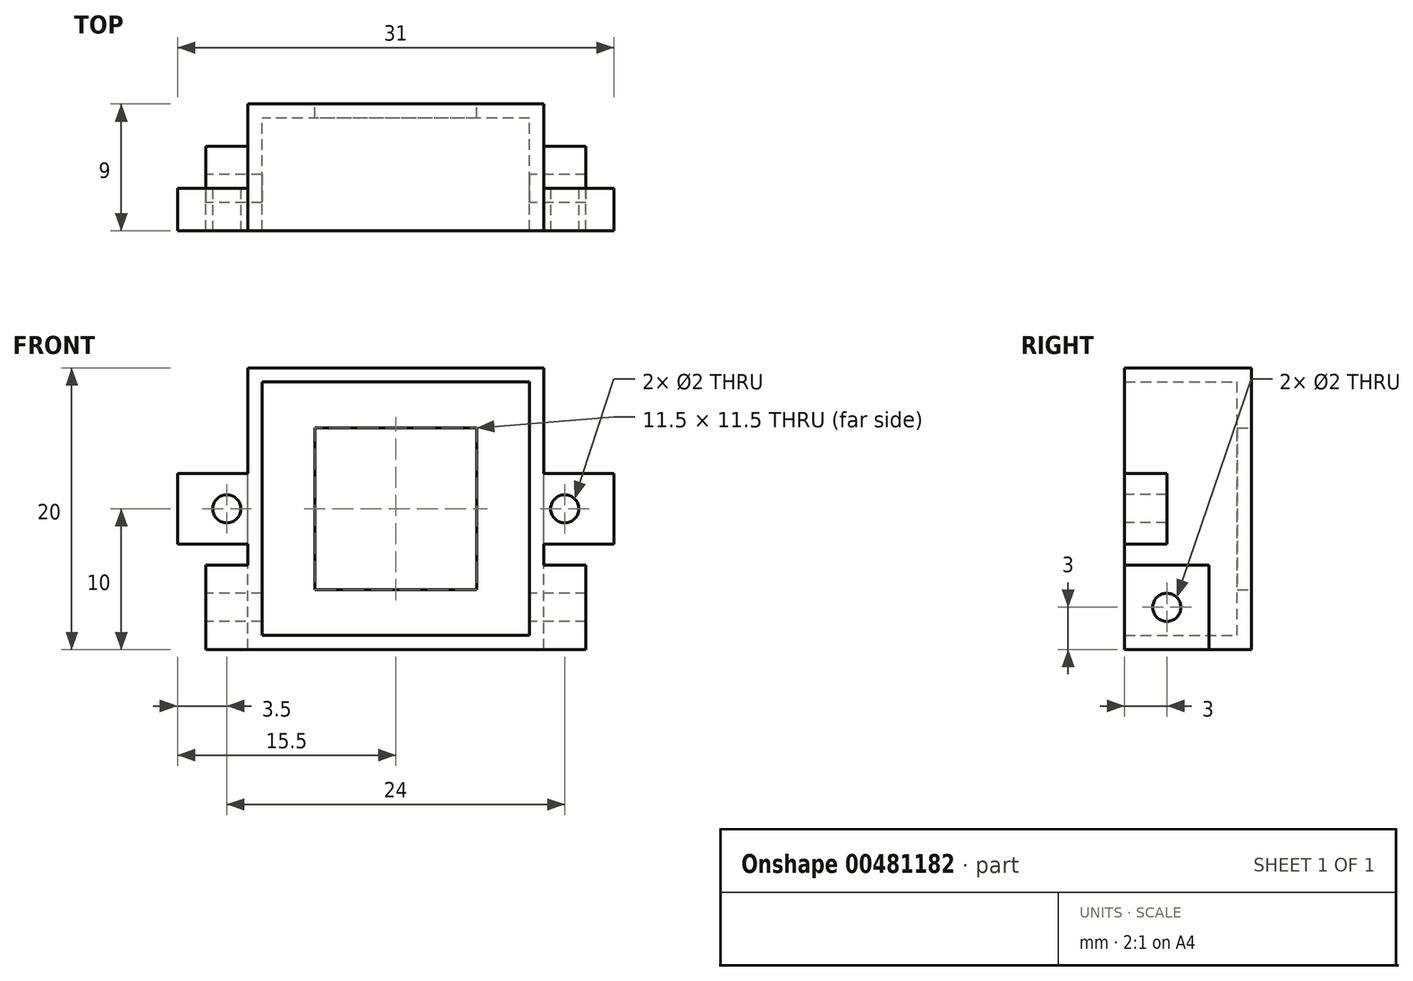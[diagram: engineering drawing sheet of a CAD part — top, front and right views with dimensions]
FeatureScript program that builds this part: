
annotation { "Feature Type Name" : "Feature", "Feature Type Description" : "" }
export const myFeature = defineFeature(function(context is Context, id is Id, definition is map)
    precondition{}
    {
        {
            var Q0;
            Q0=qCreatedBy(makeId("Front.planeOp"),FACE);
            var sketch = newSketch(context, id + "F0", { "sketchPlane" : qUnion([Q0])});
            skLineSegment(sketch, "E0.bottom", {"start": v(9, -8.5) * mm, "end": v(-9, -8.5) * mm});
            skLineSegment(sketch, "E0.top", {"start": v(9, 8.5) * mm, "end": v(-9, 8.5) * mm});
            skLineSegment(sketch, "E0.left", {"start": v(9, -8.5) * mm, "end": v(9, 8.5) * mm});
            skLineSegment(sketch, "E0.right", {"start": v(-9, -8.5) * mm, "end": v(-9, 8.5) * mm});
            skPoint(sketch, "E0.middle", {"position": v(0, 0) * mm});
            skLineSegment(sketch, "E1.bottom", {"start": v(9.5, -9) * mm, "end": v(-9.5, -9) * mm});
            skLineSegment(sketch, "E1.top", {"start": v(9.5, 9) * mm, "end": v(-9.5, 9) * mm});
            skLineSegment(sketch, "E1.left", {"start": v(9.5, -9) * mm, "end": v(9.5, 9) * mm});
            skLineSegment(sketch, "E1.right", {"start": v(-9.5, -9) * mm, "end": v(-9.5, 9) * mm});
            skLineSegment(sketch, "E2.bottom", {"start": v(10.5, -10) * mm, "end": v(-10.5, -10) * mm});
            skLineSegment(sketch, "E2.top", {"start": v(10.5, 10) * mm, "end": v(-10.5, 10) * mm});
            skLineSegment(sketch, "E2.left", {"start": v(10.5, -10) * mm, "end": v(10.5, 10) * mm});
            skLineSegment(sketch, "E2.right", {"start": v(-10.5, -10) * mm, "end": v(-10.5, 10) * mm});
            skLineSegment(sketch, "E3.bottom", {"start": v(5.75, 5.75) * mm, "end": v(-5.75, 5.75) * mm});
            skLineSegment(sketch, "E3.top", {"start": v(5.75, -5.75) * mm, "end": v(-5.75, -5.75) * mm});
            skLineSegment(sketch, "E3.left", {"start": v(5.75, 5.75) * mm, "end": v(5.75, -5.75) * mm});
            skLineSegment(sketch, "E3.right", {"start": v(-5.75, 5.75) * mm, "end": v(-5.75, -5.75) * mm});
            skSolve(sketch);
        }
        {
            var Q0;
            Q0=makeQuery(id+"F0.imprint","IMPRINT",FACE,{"disambiguationData":[TD([[makeQuery(id+"F0.imprint","IMPRINT",EDGE,{"derivedFrom":sQuery(id+"F0.wireOp",EDGE,"E0.bottom")}),-1.0]])]});
            var Q1;
            Q1=makeQuery(id+"F0.imprint","IMPRINT",FACE,{"disambiguationData":[TD([[makeQuery(id+"F0.imprint","IMPRINT",EDGE,{"derivedFrom":sQuery(id+"F0.wireOp",EDGE,"E0.bottom")}),1.0]])]});
            var Q2;
            Q2=makeQuery(id+"F0.imprint","IMPRINT",FACE,{"disambiguationData":[TD([[makeQuery(id+"F0.imprint","IMPRINT",EDGE,{"derivedFrom":sQuery(id+"F0.wireOp",EDGE,"E1.bottom")}),1.0]])]});
            extrude(context, id + "F1", {"entities" : qUnion([Q0, Q1, Q2]), "depth" : 1 * mm});
        }
        {
            var Q0;
            Q0=makeQuery(id+"F1.opExtrude","CAP_FACE",FACE,{"disambiguationData":[OSD([sQuery(id+"F0.wireOp",EDGE,"E2.bottom"),sQuery(id+"F0.wireOp",EDGE,"E2.top"),sQuery(id+"F0.wireOp",EDGE,"E2.left"),sQuery(id+"F0.wireOp",EDGE,"E2.right"),sQuery(id+"F0.wireOp",EDGE,"E3.bottom"),sQuery(id+"F0.wireOp",EDGE,"E3.top"),sQuery(id+"F0.wireOp",EDGE,"E3.left"),sQuery(id+"F0.wireOp",EDGE,"E3.right")])],"isStart":false});
            var sketch = newSketch(context, id + "F2", { "sketchPlane" : qUnion([Q0])});
            skLineSegment(sketch, "E4.bottom", {"start": v(10.5, -10) * mm, "end": v(-10.5, -10) * mm});
            skLineSegment(sketch, "E4.top", {"start": v(10.5, 10) * mm, "end": v(-10.5, 10) * mm});
            skLineSegment(sketch, "E4.left", {"start": v(10.5, -10) * mm, "end": v(10.5, 10) * mm});
            skLineSegment(sketch, "E4.right", {"start": v(-10.5, -10) * mm, "end": v(-10.5, 10) * mm});
            skPoint(sketch, "E4.middle", {"position": v(0, 0) * mm});
            skLineSegment(sketch, "E5.bottom", {"start": v(9.5, -9) * mm, "end": v(-9.5, -9) * mm});
            skLineSegment(sketch, "E5.top", {"start": v(9.5, 9) * mm, "end": v(-9.5, 9) * mm});
            skLineSegment(sketch, "E5.left", {"start": v(9.5, -9) * mm, "end": v(9.5, 9) * mm});
            skLineSegment(sketch, "E5.right", {"start": v(-9.5, -9) * mm, "end": v(-9.5, 9) * mm});
            skSolve(sketch);
        }
        {
            var Q0;
            Q0=makeQuery(id+"F2.imprint","IMPRINT",FACE,{"disambiguationData":[TD([[makeQuery(id+"F2.imprint","IMPRINT",EDGE,{"derivedFrom":sQuery(id+"F2.wireOp",EDGE,"E4.bottom")}),-1.0]])]});
            extrude(context, id + "F3", {"entities" : qUnion([Q0]), "operationType" : NewBodyOperationType.ADD, "depth" : 7 * mm});
        }
        {
            var Q0;
            Q0=makeQuery(id+"F3.opExtrude","CAP_FACE",FACE,{"disambiguationData":[OSD([sQuery(id+"F2.wireOp",EDGE,"E4.bottom"),sQuery(id+"F2.wireOp",EDGE,"E4.top"),sQuery(id+"F2.wireOp",EDGE,"E4.left"),sQuery(id+"F2.wireOp",EDGE,"E4.right"),sQuery(id+"F2.wireOp",EDGE,"E5.bottom"),sQuery(id+"F2.wireOp",EDGE,"E5.top"),sQuery(id+"F2.wireOp",EDGE,"E5.left"),sQuery(id+"F2.wireOp",EDGE,"E5.right")])],"isStart":false});
            var sketch = newSketch(context, id + "F4", { "sketchPlane" : qUnion([Q0])});
            skLineSegment(sketch, "E6.bottom", {"start": v(10.5, 10) * mm, "end": v(-10.5, 10) * mm});
            skLineSegment(sketch, "E6.top", {"start": v(10.5, -10) * mm, "end": v(-10.5, -10) * mm});
            skLineSegment(sketch, "E6.left", {"start": v(10.5, 10) * mm, "end": v(10.5, -10) * mm});
            skLineSegment(sketch, "E6.right", {"start": v(-10.5, 10) * mm, "end": v(-10.5, -10) * mm});
            skPoint(sketch, "E6.middle", {"position": v(0, 0) * mm});
            skLineSegment(sketch, "E7.bottom", {"start": v(9.5, 9) * mm, "end": v(-9.5, 9) * mm});
            skLineSegment(sketch, "E7.top", {"start": v(9.5, -9) * mm, "end": v(-9.5, -9) * mm});
            skLineSegment(sketch, "E7.left", {"start": v(9.5, 9) * mm, "end": v(9.5, -9) * mm});
            skLineSegment(sketch, "E7.right", {"start": v(-9.5, 9) * mm, "end": v(-9.5, -9) * mm});
            skPoint(sketch, "E8.middle", {"position": v(-10.5, 0) * mm});
            skPoint(sketch, "E9.middle", {"position": v(10.5, 0) * mm});
            skLineSegment(sketch, "E10.bottom", {"start": v(-10.5, -2.5) * mm, "end": v(-15.5, -2.5) * mm});
            skLineSegment(sketch, "E10.top", {"start": v(-10.5, 2.5) * mm, "end": v(-15.5, 2.5) * mm});
            skLineSegment(sketch, "E10.left", {"start": v(-10.5, -2.5) * mm, "end": v(-10.5, 2.5) * mm});
            skLineSegment(sketch, "E10.right", {"start": v(-15.5, -2.5) * mm, "end": v(-15.5, 2.5) * mm});
            skPoint(sketch, "E10.middle", {"position": v(-13, 0) * mm});
            skLineSegment(sketch, "E11.bottom", {"start": v(10.5, -2.5) * mm, "end": v(15.5, -2.5) * mm});
            skLineSegment(sketch, "E11.top", {"start": v(10.5, 2.5) * mm, "end": v(15.5, 2.5) * mm});
            skLineSegment(sketch, "E11.left", {"start": v(10.5, -2.5) * mm, "end": v(10.5, 2.5) * mm});
            skLineSegment(sketch, "E11.right", {"start": v(15.5, -2.5) * mm, "end": v(15.5, 2.5) * mm});
            skPoint(sketch, "E11.middle", {"position": v(13, 0) * mm});
            skSolve(sketch);
        }
        {
            var Q0;
            Q0=qSketchRegion(id+"F4",true);
            extrude(context, id + "F5", {"entities" : qUnion([Q0]), "operationType" : NewBodyOperationType.ADD, "depth" : 1 * mm, "hasSecondDirection" : true, "secondDirectionOppositeDirection" : true, "secondDirectionDepth" : 2 * mm});
        }
        {
            var Q0;
            Q0=makeQuery(id+"F5.opExtrude","CAP_FACE",FACE,{"disambiguationData":[OSD([sQuery(id+"F4.wireOp",EDGE,"E6.bottom"),sQuery(id+"F4.wireOp",EDGE,"E6.top"),sQuery(id+"F4.wireOp",EDGE,"E6.left"),sQuery(id+"F4.wireOp",EDGE,"E6.right"),sQuery(id+"F4.wireOp",EDGE,"E7.bottom"),sQuery(id+"F4.wireOp",EDGE,"E7.top"),sQuery(id+"F4.wireOp",EDGE,"E7.left"),sQuery(id+"F4.wireOp",EDGE,"E7.right"),sQuery(id+"F4.wireOp",EDGE,"E10.bottom"),sQuery(id+"F4.wireOp",EDGE,"E10.top"),sQuery(id+"F4.wireOp",EDGE,"E10.right"),sQuery(id+"F4.wireOp",EDGE,"E11.bottom"),sQuery(id+"F4.wireOp",EDGE,"E11.top"),sQuery(id+"F4.wireOp",EDGE,"E11.right")])],"isStart":false});
            var sketch = newSketch(context, id + "F6", { "sketchPlane" : qUnion([Q0])});
            skPoint(sketch, "E12", {"position": v(-12, 0) * mm});
            skPoint(sketch, "E13", {"position": v(12, 0) * mm});
            skSolve(sketch);
        }
        {
            var Q0;
            Q0=sQuery(id+"F6.wireOp",VERTEX,"E12");
            var Q1;
            Q1=sQuery(id+"F6.wireOp",VERTEX,"E13");
            var Q2;
            Q2=makeQuery(id+"F1.opExtrude","SWEPT_BODY",BODY,{"disambiguationData":[OSD([sQuery(id+"F0.wireOp",EDGE,"E2.bottom"),sQuery(id+"F0.wireOp",EDGE,"E2.top"),sQuery(id+"F0.wireOp",EDGE,"E2.left"),sQuery(id+"F0.wireOp",EDGE,"E2.right"),sQuery(id+"F0.wireOp",EDGE,"E3.bottom"),sQuery(id+"F0.wireOp",EDGE,"E3.top"),sQuery(id+"F0.wireOp",EDGE,"E3.left"),sQuery(id+"F0.wireOp",EDGE,"E3.right")])]});
            hole(context, id + "F7", {"style" : HoleStyle.SIMPLE, "endStyle" : HoleEndStyle.THROUGH, "holeDiameter" : 2 * mm, "isTappedThrough" : true, "tappedDepth" : 12 * mm, "tapClearance" : 3, "locations" : qUnion([Q0, Q1]), "scope" : qUnion([Q2])});
        }
        {
            var Q0;
            {var subQ0=sQuery(id+"F4.wireOp",EDGE,"E6.right");Q0=makeQuery(id+"F5.boolean.opBoolean","MERGE",FACE,{"derivedFrom":[makeQuery(id+"F3.boolean.opBoolean","MERGE",FACE,{"derivedFrom":[makeQuery(id+"F1.opExtrude","SWEPT_FACE",FACE,{"disambiguationData":[OSD([sQuery(id+"F0.wireOp",EDGE,"E2.right")])]}),makeQuery(id+"F3.opExtrude","SWEPT_FACE",FACE,{"disambiguationData":[OSD([sQuery(id+"F2.wireOp",EDGE,"E4.right")])]})]}),makeQuery(id+"F5.opExtrude","SWEPT_FACE",FACE,{"disambiguationData":[OSD([subQ0]),TDD([makeQuery(id+"F4.imprint","IMPRINT",EDGE,{"disambiguationData":[TD([[makeQuery(id+"F4.imprint","INTERSECT",VERTEX,{"derivedFrom":[sQuery(id+"F4.wireOp",EDGE,"E6.top"),subQ0]}),-1.0]])],"derivedFrom":subQ0})])]}),makeQuery(id+"F5.opExtrude","SWEPT_FACE",FACE,{"disambiguationData":[OSD([subQ0]),TDD([makeQuery(id+"F4.imprint","IMPRINT",EDGE,{"disambiguationData":[TD([[makeQuery(id+"F4.imprint","INTERSECT",VERTEX,{"derivedFrom":[sQuery(id+"F4.wireOp",EDGE,"E6.bottom"),subQ0]}),1.0]])],"derivedFrom":subQ0})])]})]});}
            var sketch = newSketch(context, id + "F8", { "sketchPlane" : qUnion([Q0])});
            skLineSegment(sketch, "E14.bottom", {"start": v(9, -10) * mm, "end": v(3, -10) * mm});
            skLineSegment(sketch, "E14.top", {"start": v(9, -4) * mm, "end": v(3, -4) * mm});
            skLineSegment(sketch, "E14.left", {"start": v(9, -10) * mm, "end": v(9, -4) * mm});
            skLineSegment(sketch, "E14.right", {"start": v(3, -10) * mm, "end": v(3, -4) * mm});
            skSolve(sketch);
        }
        {
            var Q0;
            Q0=makeQuery(id+"F8.imprint","IMPRINT",FACE,{"disambiguationData":[TD([[makeQuery(id+"F8.imprint","IMPRINT",EDGE,{"derivedFrom":sQuery(id+"F8.wireOp",EDGE,"E14.bottom")}),-1.0]])]});
            extrude(context, id + "F9", {"entities" : qUnion([Q0]), "operationType" : NewBodyOperationType.ADD, "depth" : 3 * mm});
        }
        {
            var Q0;
            {var subQ0=sQuery(id+"F4.wireOp",EDGE,"E6.left");Q0=makeQuery(id+"F5.boolean.opBoolean","MERGE",FACE,{"derivedFrom":[makeQuery(id+"F3.boolean.opBoolean","MERGE",FACE,{"derivedFrom":[makeQuery(id+"F1.opExtrude","SWEPT_FACE",FACE,{"disambiguationData":[OSD([sQuery(id+"F0.wireOp",EDGE,"E2.left")])]}),makeQuery(id+"F3.opExtrude","SWEPT_FACE",FACE,{"disambiguationData":[OSD([sQuery(id+"F2.wireOp",EDGE,"E4.left")])]})]}),makeQuery(id+"F5.opExtrude","SWEPT_FACE",FACE,{"disambiguationData":[OSD([subQ0]),TDD([makeQuery(id+"F4.imprint","IMPRINT",EDGE,{"disambiguationData":[TD([[makeQuery(id+"F4.imprint","INTERSECT",VERTEX,{"derivedFrom":[sQuery(id+"F4.wireOp",EDGE,"E6.top"),subQ0]}),-1.0]])],"derivedFrom":subQ0})])]}),makeQuery(id+"F5.opExtrude","SWEPT_FACE",FACE,{"disambiguationData":[OSD([subQ0]),TDD([makeQuery(id+"F4.imprint","IMPRINT",EDGE,{"disambiguationData":[TD([[makeQuery(id+"F4.imprint","INTERSECT",VERTEX,{"derivedFrom":[sQuery(id+"F4.wireOp",EDGE,"E6.bottom"),subQ0]}),1.0]])],"derivedFrom":subQ0})])]})]});}
            var sketch = newSketch(context, id + "F10", { "sketchPlane" : qUnion([Q0])});
            skLineSegment(sketch, "E15.bottom", {"start": v(-9, -10) * mm, "end": v(-3, -10) * mm});
            skLineSegment(sketch, "E15.top", {"start": v(-9, -4) * mm, "end": v(-3, -4) * mm});
            skLineSegment(sketch, "E15.left", {"start": v(-9, -10) * mm, "end": v(-9, -4) * mm});
            skLineSegment(sketch, "E15.right", {"start": v(-3, -10) * mm, "end": v(-3, -4) * mm});
            skSolve(sketch);
        }
        {
            var Q0;
            Q0=makeQuery(id+"F10.imprint","IMPRINT",FACE,{"disambiguationData":[TD([[makeQuery(id+"F10.imprint","IMPRINT",EDGE,{"derivedFrom":sQuery(id+"F10.wireOp",EDGE,"E15.bottom")}),1.0]])]});
            extrude(context, id + "F11", {"entities" : qUnion([Q0]), "operationType" : NewBodyOperationType.ADD, "depth" : 3 * mm});
        }
        {
            var Q0;
            Q0=makeQuery(id+"F9.opExtrude","CAP_FACE",FACE,{"disambiguationData":[OSD([sQuery(id+"F8.wireOp",EDGE,"E14.bottom"),sQuery(id+"F8.wireOp",EDGE,"E14.top"),sQuery(id+"F8.wireOp",EDGE,"E14.left"),sQuery(id+"F8.wireOp",EDGE,"E14.right")])],"isStart":false});
            var sketch = newSketch(context, id + "F12", { "sketchPlane" : qUnion([Q0])});
            skPoint(sketch, "E16", {"position": v(6, -7) * mm});
            skSolve(sketch);
        }
        {
            var Q0;
            Q0=sQuery(id+"F12.wireOp",VERTEX,"E16");
            var Q1;
            Q1=makeQuery(id+"F1.opExtrude","SWEPT_BODY",BODY,{"disambiguationData":[OSD([sQuery(id+"F0.wireOp",EDGE,"E2.bottom"),sQuery(id+"F0.wireOp",EDGE,"E2.top"),sQuery(id+"F0.wireOp",EDGE,"E2.left"),sQuery(id+"F0.wireOp",EDGE,"E2.right"),sQuery(id+"F0.wireOp",EDGE,"E3.bottom"),sQuery(id+"F0.wireOp",EDGE,"E3.top"),sQuery(id+"F0.wireOp",EDGE,"E3.left"),sQuery(id+"F0.wireOp",EDGE,"E3.right")])]});
            hole(context, id + "F13", {"style" : HoleStyle.SIMPLE, "endStyle" : HoleEndStyle.THROUGH, "holeDiameter" : 2 * mm, "isTappedThrough" : true, "tappedDepth" : 12 * mm, "tapClearance" : 3, "locations" : qUnion([Q0]), "scope" : qUnion([Q1])});
        }
    });
